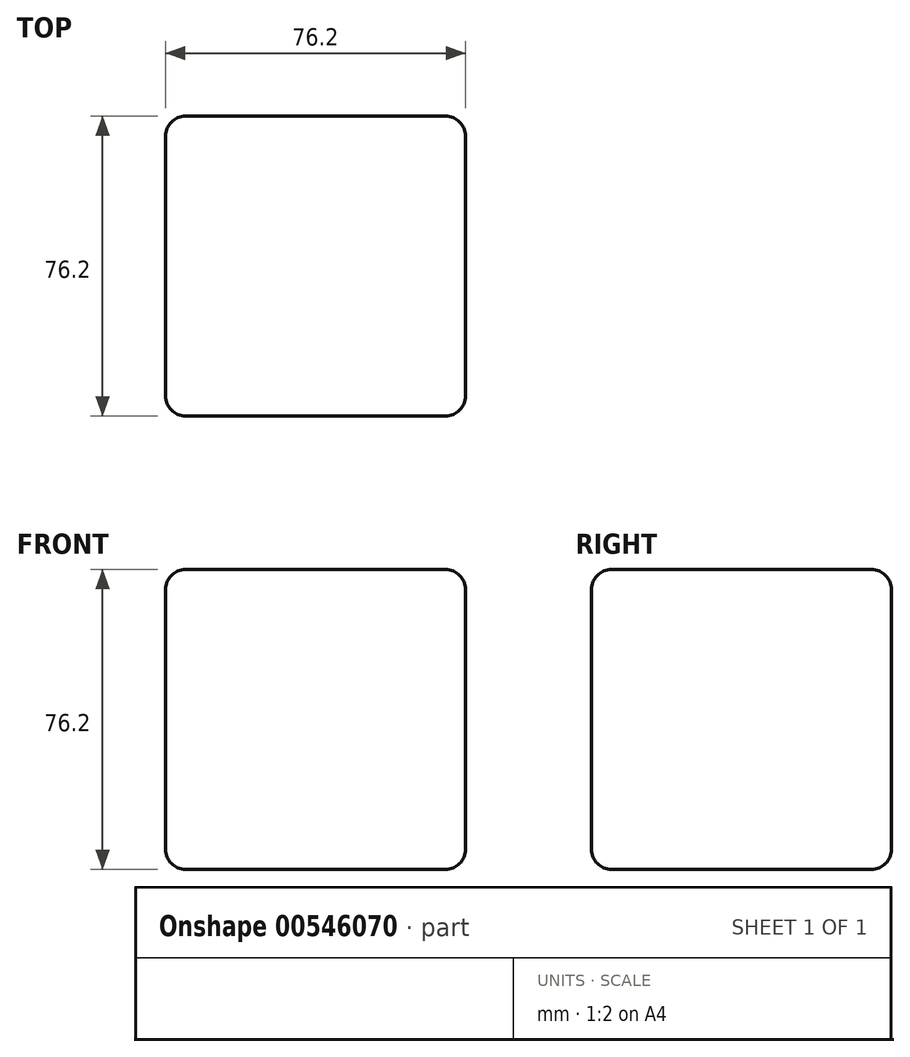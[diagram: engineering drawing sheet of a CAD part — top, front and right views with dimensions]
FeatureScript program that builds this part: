
annotation { "Feature Type Name" : "Feature", "Feature Type Description" : "" }
export const myFeature = defineFeature(function(context is Context, id is Id, definition is map)
    precondition{}
    {
        {
            var Q0;
            Q0=qCreatedBy(makeId("Top.planeOp"),FACE);
            var sketch = newSketch(context, id + "F0", { "sketchPlane" : qUnion([Q0])});
            skPoint(sketch, "E0.0.midPoint", {"position": v(0, 68.16) * mm});
            skPoint(sketch, "E0.5.end.orphan", {"position": v(-39.35, 68.16) * mm});
            skPoint(sketch, "E0.cCircle.center.orphan", {"position": v(0, 0) * mm});
            skPoint(sketch, "E0.1.start.orphan", {"position": v(39.35, 68.16) * mm});
            skLineSegment(sketch, "E1.bottom", {"start": v(-50.8, 25.4) * mm, "end": v(25.4, 25.4) * mm});
            skLineSegment(sketch, "E1.top", {"start": v(-50.8, -50.8) * mm, "end": v(25.4, -50.8) * mm});
            skLineSegment(sketch, "E1.left", {"start": v(-50.8, 25.4) * mm, "end": v(-50.8, -50.8) * mm});
            skLineSegment(sketch, "E1.right", {"start": v(25.4, 25.4) * mm, "end": v(25.4, -50.8) * mm});
            skPoint(sketch, "E2.end.orphan", {"position": v(-50.8, 0) * mm});
            skSolve(sketch);
        }
        {
            var Q0;
            Q0 = qSketchRegion(id + "F0", true);
            extrude(context, id + "F1", {"entities" : qUnion([Q0]), "depth" : 76.2 * mm, "offsetDistance" : 25.4 * mm});
        }
        {
            var Q0;
            Q0=makeQuery(id+"F1.opExtrude","CAP_EDGE",EDGE,{"disambiguationData":[OSD([sQuery(id+"F0.wireOp",EDGE,"E1.right")])],"isStart":false});
            var Q1;
            Q1=makeQuery(id+"F1.opExtrude","CAP_EDGE",EDGE,{"disambiguationData":[OSD([sQuery(id+"F0.wireOp",EDGE,"E1.left")])],"isStart":false});
            var Q2;
            Q2=makeQuery(id+"F1.opExtrude","CAP_EDGE",EDGE,{"disambiguationData":[OSD([sQuery(id+"F0.wireOp",EDGE,"E1.top")])],"isStart":false});
            var Q3;
            Q3=makeQuery(id+"F1.opExtrude","CAP_EDGE",EDGE,{"disambiguationData":[OSD([sQuery(id+"F0.wireOp",EDGE,"E1.bottom")])],"isStart":false});
            var Q4;
            Q4=makeQuery(id+"F1.opExtrude","SWEPT_EDGE",EDGE,{"disambiguationData":[OSD([sQuery(id+"F0.wireOp",EDGE,"E1.top"),sQuery(id+"F0.wireOp",EDGE,"E1.right")])]});
            var Q5;
            Q5=makeQuery(id+"F1.opExtrude","SWEPT_EDGE",EDGE,{"disambiguationData":[OSD([sQuery(id+"F0.wireOp",EDGE,"E1.bottom"),sQuery(id+"F0.wireOp",EDGE,"E1.right")])]});
            var Q6;
            Q6=makeQuery(id+"F1.opExtrude","SWEPT_FACE",FACE,{"disambiguationData":[OSD([sQuery(id+"F0.wireOp",EDGE,"E1.bottom")])]});
            var Q7;
            Q7=makeQuery(id+"F1.opExtrude","SWEPT_EDGE",EDGE,{"disambiguationData":[OSD([sQuery(id+"F0.wireOp",EDGE,"E1.top"),sQuery(id+"F0.wireOp",EDGE,"E1.left")])]});
            var Q8;
            Q8=makeQuery(id+"F1.opExtrude","CAP_EDGE",EDGE,{"disambiguationData":[OSD([sQuery(id+"F0.wireOp",EDGE,"E1.right")])],"isStart":true});
            var Q9;
            Q9=makeQuery(id+"F1.opExtrude","CAP_EDGE",EDGE,{"disambiguationData":[OSD([sQuery(id+"F0.wireOp",EDGE,"E1.left")])],"isStart":true});
            var Q10;
            Q10=makeQuery(id+"F1.opExtrude","CAP_EDGE",EDGE,{"disambiguationData":[OSD([sQuery(id+"F0.wireOp",EDGE,"E1.top")])],"isStart":true});
            fillet(context, id + "F2", {"entities" : qUnion([Q0, Q1, Q2, Q3, Q4, Q5, Q6, Q7, Q8, Q9, Q10]), "radius" : 5.08 * mm, "tangentPropagation" : true, "allowEdgeOverflow" : false});
        }
    });
